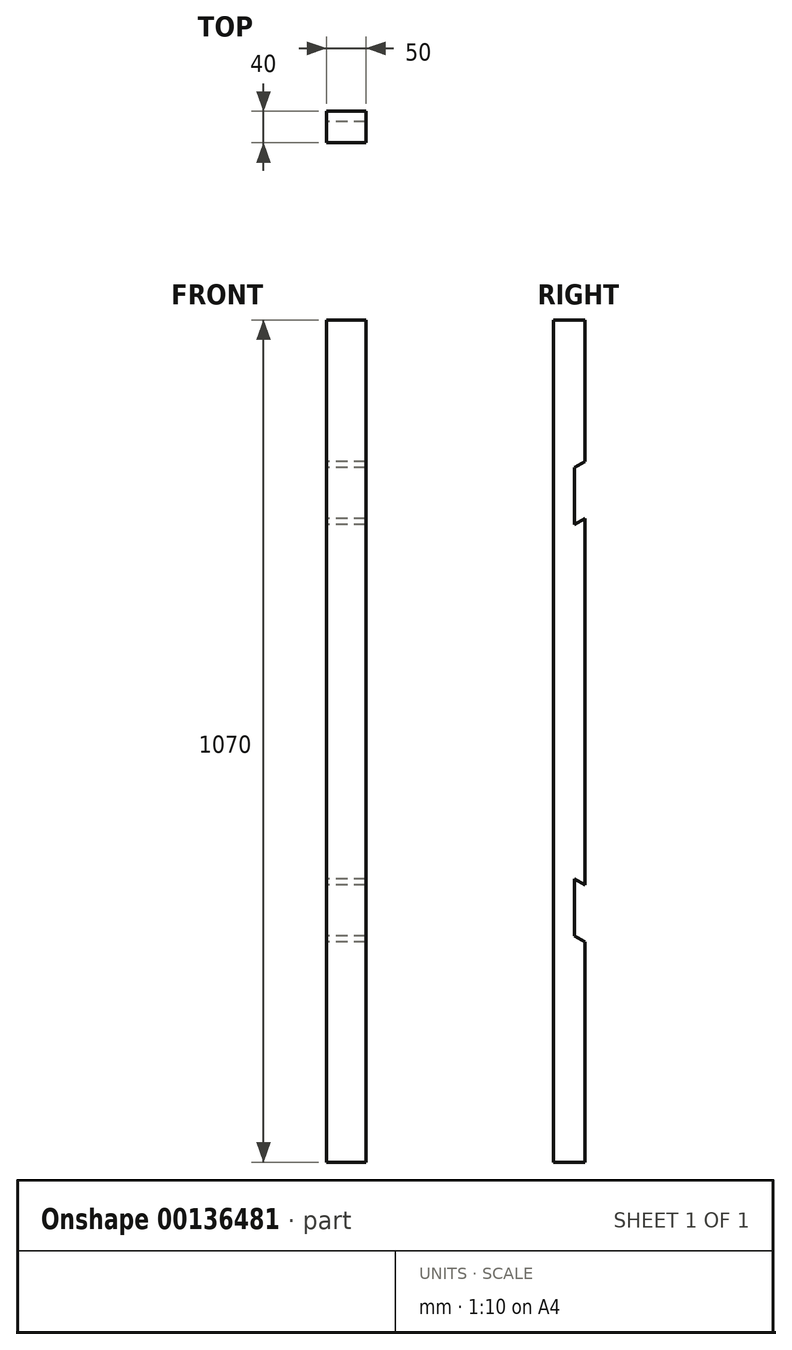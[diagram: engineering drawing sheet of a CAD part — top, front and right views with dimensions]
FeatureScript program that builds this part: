
annotation { "Feature Type Name" : "Feature", "Feature Type Description" : "" }
export const myFeature = defineFeature(function(context is Context, id is Id, definition is map)
    precondition{}
    {
        {
            assignVariable(context, id + "F0", {"name" : "Picket_X", "anyValue" : 50});
        }
        {
            var Q0;
            Q0=qCreatedBy(makeId("Right.planeOp"),FACE);
            var sketch = newSketch(context, id + "F1", { "sketchPlane" : qUnion([Q0])});
            skLineSegment(sketch, "E0.top", {"start": v(-26.67, 220) * mm, "end": v(-66.67, 220) * mm});
            skLineSegment(sketch, "E0.right", {"start": v(-66.67, -850) * mm, "end": v(-66.67, 220) * mm});
            skPoint(sketch, "E0.middle", {"position": v(0, 0) * mm});
            skLineSegment(sketch, "E1", {"start": v(-40, 32.3) * mm, "end": v(-40, -40) * mm});
            skLineSegment(sketch, "E2", {"start": v(-40, -40) * mm, "end": v(-26.67, -32.3) * mm});
            skLineSegment(sketch, "E3", {"start": v(-26.67, 40) * mm, "end": v(-26.67, 220) * mm});
            skLineSegment(sketch, "E4", {"start": v(-26.67, -32.3) * mm, "end": v(-26.67, -497.7) * mm});
            skLineSegment(sketch, "E5", {"start": v(-26.67, 40) * mm, "end": v(-26.67, -32.3) * mm, "construction": true});
            skLineSegment(sketch, "E6.bottom", {"start": v(40, 40) * mm, "end": v(-40, 40) * mm, "construction": true});
            skLineSegment(sketch, "E6.top", {"start": v(40, -40) * mm, "end": v(-40, -40) * mm, "construction": true});
            skLineSegment(sketch, "E6.right", {"start": v(-40, 40) * mm, "end": v(-40, -40) * mm, "construction": true});
            skLineSegment(sketch, "E7", {"start": v(88.56, -265) * mm, "end": v(-221.89, -265) * mm, "construction": true});
            skPoint(sketch, "E8", {"position": v(-66.67, -265) * mm});
            skLineSegment(sketch, "E9", {"start": v(-26.67, -570) * mm, "end": v(-26.67, -850) * mm});
            skLineSegment(sketch, "E10", {"start": v(-26.67, -850) * mm, "end": v(-66.67, -850) * mm});
            skLineSegment(sketch, "E11", {"start": v(40, 40) * mm, "end": v(40, -40) * mm, "construction": true});
            skLineSegment(sketch, "E12.MirrorCS", {"start": v(-40, -490) * mm, "end": v(-26.67, -497.7) * mm});
            skLineSegment(sketch, "E13.MirrorCS", {"start": v(-40, -570) * mm, "end": v(-40, -490) * mm, "construction": true});
            skLineSegment(sketch, "E14.MirrorCS", {"start": v(-40, -562.3) * mm, "end": v(-40, -490) * mm});
            skLineSegment(sketch, "E15.MirrorCS", {"start": v(40, -570) * mm, "end": v(40, -490) * mm, "construction": true});
            skLineSegment(sketch, "E16.MirrorCS", {"start": v(-26.67, -570) * mm, "end": v(-40, -562.3) * mm});
            skLineSegment(sketch, "E17.MirrorCS", {"start": v(40, -490) * mm, "end": v(-40, -490) * mm, "construction": true});
            skLineSegment(sketch, "E18.MirrorCS", {"start": v(40, -570) * mm, "end": v(-40, -570) * mm, "construction": true});
            skLineSegment(sketch, "E19.MirrorCS", {"start": v(-26.67, -570) * mm, "end": v(-26.67, -497.7) * mm, "construction": true});
            skLineSegment(sketch, "E20", {"start": v(40, 40) * mm, "end": v(0, 0) * mm, "construction": true});
            skLineSegment(sketch, "E21", {"start": v(0, 0) * mm, "end": v(-40, -40) * mm, "construction": true});
            skLineSegment(sketch, "E22", {"start": v(-26.67, 40) * mm, "end": v(-40, 32.3) * mm});
            skSolve(sketch);
        }
        {
            var Q0;
            {var subQ2=sQuery(id+"F1.wireOp",EDGE,"E0.top");Q0=makeQuery(id+"F1.imprint","IMPRINT",FACE,{"disambiguationData":[TD([[makeQuery(id+"F1.imprint","IMPRINT",EDGE,{"derivedFrom":subQ2}),1.0]])]});}
            var Q1;
            {var subQ0=sQuery(id+"F1.wireOp",EDGE,"E3");var subQ1=sQuery(id+"F1.wireOp",EDGE,"cWGawI1q-kyB3-GyzM-JcFa-jFvkeEIJsHIR");var subQ2=makeQuery(id+"F1.imprint","INTERSECT",VERTEX,{"derivedFrom":[subQ1,subQ0]});Q1=makeQuery(id+"F1.imprint","IMPRINT",FACE,{"disambiguationData":[TD([[makeQuery(id+"F1.imprint","IMPRINT",EDGE,{"disambiguationData":[TD([[subQ2,-1.0]])],"derivedFrom":subQ1}),-1.0]])]});}
            var Q2;
            {var subQ0=sQuery(id+"F1.wireOp",EDGE,"aBrPsMud-MBQY-V48I-gAYi-u8uMVLHz42j3");var subQ1=sQuery(id+"F1.wireOp",EDGE,"E2");var subQ2=makeQuery(id+"F1.imprint","INTERSECT",VERTEX,{"derivedFrom":[subQ1,subQ0]});Q2=makeQuery(id+"F1.imprint","IMPRINT",FACE,{"disambiguationData":[TD([[makeQuery(id+"F1.imprint","IMPRINT",EDGE,{"disambiguationData":[TD([[subQ2,-1.0]])],"derivedFrom":subQ1}),-1.0]])]});}
            var Q3;
            {var subQ0=sQuery(id+"F1.wireOp",EDGE,"7c64dacc-8125-4eb5-b731-666fbb44cb6d7.MirrorCS");var subQ1=sQuery(id+"F1.wireOp",EDGE,"7c64dacc-8125-4eb5-b731-666fbb44cb6d0.MirrorCS");var subQ2=makeQuery(id+"F1.imprint","INTERSECT",VERTEX,{"derivedFrom":[subQ1,subQ0]});Q3=makeQuery(id+"F1.imprint","IMPRINT",FACE,{"disambiguationData":[TD([[makeQuery(id+"F1.imprint","IMPRINT",EDGE,{"disambiguationData":[TD([[subQ2,1.0]])],"derivedFrom":subQ1}),-1.0]])]});}
            var Q4;
            {var subQ0=sQuery(id+"F1.wireOp",EDGE,"E16.MirrorCS");var subQ1=sQuery(id+"F1.wireOp",EDGE,"E9");var subQ2=makeQuery(id+"F1.imprint","INTERSECT",VERTEX,{"derivedFrom":[subQ1,subQ0]});Q4=makeQuery(id+"F1.imprint","IMPRINT",FACE,{"disambiguationData":[TD([[makeQuery(id+"F1.imprint","IMPRINT",EDGE,{"disambiguationData":[TD([[subQ2,-1.0]])],"derivedFrom":subQ1}),-1.0]])]});}
            extrude(context, id + "F2", {"entities" : qUnion([Q0, Q1, Q2, Q3, Q4]), "depth" : (getVariable(context, 'Picket_X')) * mm});
        }
    });
